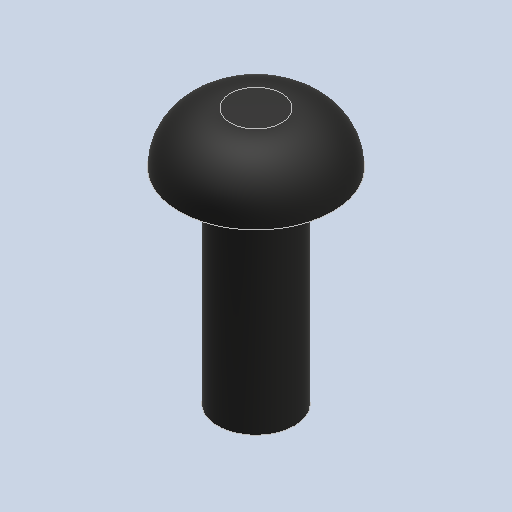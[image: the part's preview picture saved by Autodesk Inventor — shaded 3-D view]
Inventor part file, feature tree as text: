
AUTODESK INVENTOR PART (.ipt)
format: ipt  version: 2023 (Build 270158030, 158C)  size: 125,440 bytes
history: native  units: mm
features: extrude x2, sketch x2, other x1, fillet x1
ambient origin geometry x8: Origin, YZ Plane, XZ Plane, XY Plane, X Axis, Y Axis, Z Axis, Center Point
bodies: Body1 (feature_tree)
feature tree (6):
  other  "ソリッド1"
  extrude  "押し出し1"  Depth=3.0mm
  extrude  "押し出し2"  Depth=8.0mm TaperAngle=0.0deg
  fillet  "フィレット1"  Radius=6.0mm
  sketch  "スケッチ1"
  sketch  "スケッチ2"
